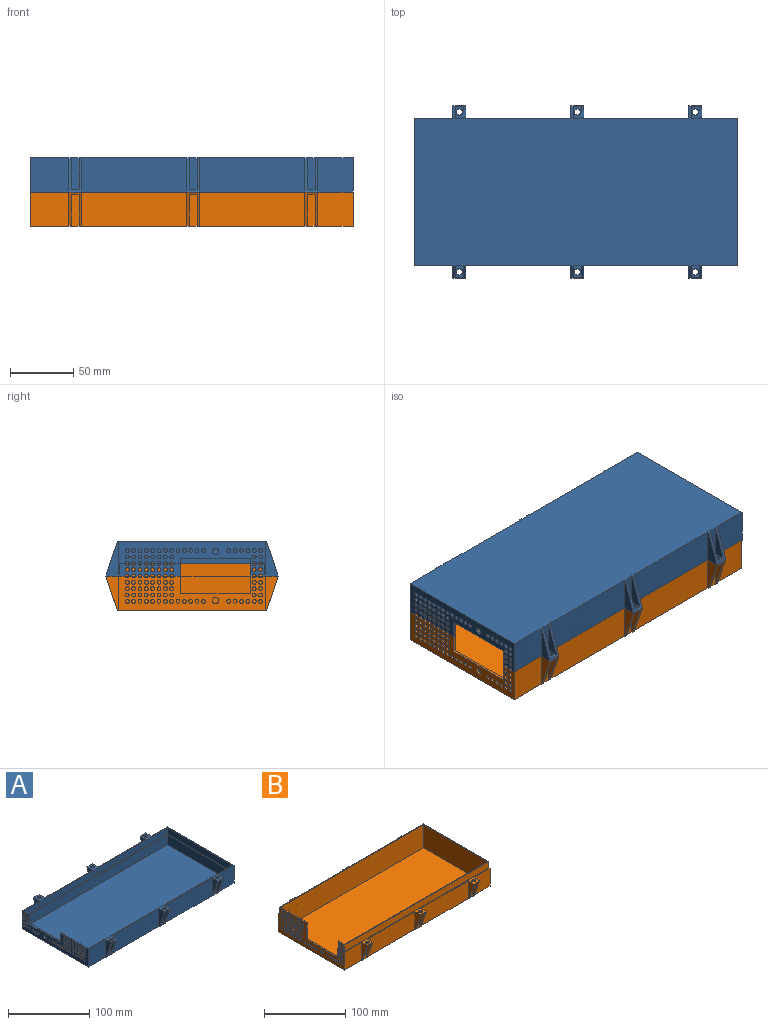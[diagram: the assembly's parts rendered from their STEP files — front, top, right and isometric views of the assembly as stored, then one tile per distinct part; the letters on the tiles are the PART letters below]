
ASSEMBLY  parts=2 mates=1
PART A: 154 faces, bbox 254x136x27 mm
  f0: plane 252.2x114.2mm, normal (0,0,1), area 671.6mm2, adj f20,f23,f41,f42,f43,f44,f45,f46
  f1: plane 2x1.2mm, normal (0,0,1), area 2.4mm2, adj f20,f23,f108,f109
  f2: plane 2x1.2mm, normal (0,0,1), area 2.4mm2, adj f20,f23,f107,f108
  f3: plane 2x1.2mm, normal (0,0,1), area 2.4mm2, adj f20,f23,f106,f107
  f4: plane 2x1.2mm, normal (0,0,1), area 2.4mm2, adj f20,f23,f105,f106
  f5: plane 2x1.2mm, normal (0,0,1), area 2.4mm2, adj f20,f23,f104,f105
  f6: plane 2x1.2mm, normal (0,0,1), area 2.4mm2, adj f20,f23,f103,f104
  f7: plane 2x1.2mm, normal (0,0,1), area 2.4mm2, adj f20,f23,f102,f103
  f8: plane 1.5x1.2mm, normal (0,0,1), area 1.8mm2, adj f20,f44,f93,f96
  f9: plane 2x1.2mm, normal (0,0,1), area 2.4mm2, adj f20,f44,f95,f96
  f10: plane 1.5x0.9mm, normal (0,0,1), area 1.3mm2, adj f37,f44,f93,f100
  f11: plane 2x0.9mm, normal (0,0,1), area 1.8mm2, adj f37,f44,f98,f100
  f12: plane 2x0.9mm, normal (0,0,1), area 1.8mm2, adj f23,f37,f134,f140
  f13: plane 2x0.9mm, normal (0,0,1), area 1.8mm2, adj f23,f37,f138,f140
  f14: plane 254x136mm, normal (0,0,1), area 1047.8mm2, adj f23,f25,f27,f29,f30,f32,f34,f36
  f15: plane 2x0.9mm, normal (0,0,1), area 1.8mm2, adj f23,f37,f134,f136
  f16: plane 2x0.9mm, normal (0,0,1), area 1.8mm2, adj f23,f37,f127,f132
  f17: plane 2x0.9mm, normal (0,0,1), area 1.8mm2, adj f23,f37,f130,f132
  f18: plane 2x0.9mm, normal (0,0,1), area 1.8mm2, adj f23,f37,f129,f138
  f19: plane 2x0.9mm, normal (0,0,1), area 1.8mm2, adj f23,f37,f127,f129
  f20: plane 112x15mm, normal (1,0,0), area 1200mm2, adj f0,f1,f2,f3,f4,f5,f6,f7
  f21: plane 5.5x1.2mm, normal (0,0,1), area 6.6mm2, adj f20,f23,f92,f102
  f22: plane 5.5x0.9mm, normal (0,0,1), area 4.9mm2, adj f23,f37,f92,f130
  f23: plane 48.1x10mm, normal (1,0,0), area 367.9mm2, adj f0,f1,f2,f3,f4,f5,f6,f7
  f24: plane 25x6mm, normal (0,1,0), area 150mm2, adj f40,f84,f88,f89
  f25: plane 28x27mm, normal (0,1,0), area 756mm2, adj f14,f39,f40,f87
  f26: plane 25x6mm, normal (0,1,0), area 150mm2, adj f40,f77,f81,f82
  f27: plane 83x27mm, normal (0,1,0), area 2241mm2, adj f14,f40,f80,f85
  f28: plane 25x6mm, normal (0,1,0), area 150mm2, adj f40,f70,f74,f75
  f29: plane 83x27mm, normal (0,1,0), area 2241mm2, adj f14,f40,f73,f78
  f30: plane 28x27mm, normal (0,-1,0), area 756mm2, adj f14,f39,f40,f66
  f31: plane 25x6mm, normal (0,-1,0), area 150mm2, adj f40,f63,f67,f68
  f32: plane 83x27mm, normal (0,-1,0), area 2241mm2, adj f14,f40,f59,f64
  f33: plane 25x6mm, normal (0,-1,0), area 150mm2, adj f40,f56,f60,f61
  f34: plane 83x27mm, normal (0,-1,0), area 2241mm2, adj f14,f40,f52,f57
  f35: plane 25x6mm, normal (0,-1,0), area 150mm2, adj f40,f49,f53,f54
  f36: plane 30x27mm, normal (0,1,0), area 810mm2, adj f14,f37,f40,f71
  f37: plane 116x27mm, normal (-1,0,0), area 1960.7mm2, adj f10,f11,f12,f13,f14,f15,f16,f17
  f38: plane 30x27mm, normal (0,-1,0), area 810mm2, adj f14,f37,f40,f50
  f39: plane 116x27mm, normal (1,0,0), area 3132mm2, adj f14,f25,f30,f40
  f40: plane 254x117.41mm, normal (0,0,-1), area 29480.9mm2, adj f24,f25,f26,f27,f28,f29,f30,f31
  f41: plane 252.2x10mm, normal (0,1,0), area 2522mm2, adj f0,f14,f23,f42
  f42: plane 114.2x10mm, normal (-1,0,0), area 1142mm2, adj f0,f14,f41,f43
  f43: plane 252.2x10mm, normal (0,-1,0), area 2522mm2, adj f0,f14,f42,f44
  f44: plane 11.1x10mm, normal (1,0,0), area 82.7mm2, adj f0,f8,f9,f10,f11,f14,f43,f93
  f45: plane 250x15mm, normal (0,1,0), area 3750mm2, adj f0,f20,f46,f48
  f46: plane 112x15mm, normal (-1,0,0), area 1680mm2, adj f0,f45,f47,f48
  f47: plane 250x15mm, normal (0,-1,0), area 3750mm2, adj f0,f20,f46,f48
  f48: plane 250x112mm, normal (0,0,1), area 28000mm2, adj f20,f45,f46,f47
  f49: plane 9.31x6mm, normal (0,0,-1), area 36.2mm2, adj f35,f51,f53,f54,f55
  f50: plane 27x10mm, normal (-1,0,0), area 144.5mm2, adj f14,f38,f40,f51
  f51: plane 27x10mm, normal (0,-0.95,-0.33), area 126.9mm2, adj f14,f40,f49,f50,f52,f53,f54
  f52: plane 27x10mm, normal (1,0,0), area 144.5mm2, adj f14,f34,f40,f51
  f53: plane 25x9.31mm, normal (1,0,0), area 125.2mm2, adj f35,f40,f49,f51
  f54: plane 25x9.31mm, normal (-1,0,0), area 125.2mm2, adj f35,f40,f49,f51
  f55: cylinder r=2.5mm len=5mm, axis (0,0,1), area 31.4mm2, adj f14,f49
  f56: plane 9.31x6mm, normal (0,0,-1), area 36.2mm2, adj f33,f58,f60,f61,f62
  f57: plane 27x10mm, normal (-1,0,0), area 144.5mm2, adj f14,f34,f40,f58
  f58: plane 27x10mm, normal (0,-0.95,-0.33), area 126.9mm2, adj f14,f40,f56,f57,f59,f60,f61
  f59: plane 27x10mm, normal (1,0,0), area 144.5mm2, adj f14,f32,f40,f58
  f60: plane 25x9.31mm, normal (1,0,0), area 125.2mm2, adj f33,f40,f56,f58
  f61: plane 25x9.31mm, normal (-1,0,0), area 125.2mm2, adj f33,f40,f56,f58
  f62: cylinder r=2.5mm len=5mm, axis (0,0,1), area 31.4mm2, adj f14,f56
  f63: plane 9.31x6mm, normal (0,0,-1), area 36.2mm2, adj f31,f65,f67,f68,f69
  f64: plane 27x10mm, normal (-1,0,0), area 144.5mm2, adj f14,f32,f40,f65
  f65: plane 27x10mm, normal (0,-0.95,-0.33), area 126.9mm2, adj f14,f40,f63,f64,f66,f67,f68
  f66: plane 27x10mm, normal (1,0,0), area 144.5mm2, adj f14,f30,f40,f65
  f67: plane 25x9.31mm, normal (1,0,0), area 125.2mm2, adj f31,f40,f63,f65
  f68: plane 25x9.31mm, normal (-1,0,0), area 125.2mm2, adj f31,f40,f63,f65
  f69: cylinder r=2.5mm len=5mm, axis (0,0,1), area 31.4mm2, adj f14,f63
  f70: plane 9.31x6mm, normal (0,0,-1), area 36.2mm2, adj f28,f72,f74,f75,f76
  f71: plane 27x10mm, normal (-1,0,0), area 144.5mm2, adj f14,f36,f40,f72
  f72: plane 27x10mm, normal (0,0.95,-0.33), area 126.9mm2, adj f14,f40,f70,f71,f73,f74,f75
  f73: plane 27x10mm, normal (1,0,0), area 144.5mm2, adj f14,f29,f40,f72
  f74: plane 25x9.31mm, normal (1,0,0), area 125.2mm2, adj f28,f40,f70,f72
  f75: plane 25x9.31mm, normal (-1,0,0), area 125.2mm2, adj f28,f40,f70,f72
  f76: cylinder r=2.5mm len=5mm, axis (0,0,1), area 31.4mm2, adj f14,f70
  f77: plane 9.31x6mm, normal (0,0,-1), area 36.2mm2, adj f26,f79,f81,f82,f83
  f78: plane 27x10mm, normal (-1,0,0), area 144.5mm2, adj f14,f29,f40,f79
  f79: plane 27x10mm, normal (0,0.95,-0.33), area 126.9mm2, adj f14,f40,f77,f78,f80,f81,f82
  f80: plane 27x10mm, normal (1,0,0), area 144.5mm2, adj f14,f27,f40,f79
  f81: plane 25x9.31mm, normal (1,0,0), area 125.2mm2, adj f26,f40,f77,f79
  f82: plane 25x9.31mm, normal (-1,0,0), area 125.2mm2, adj f26,f40,f77,f79
  f83: cylinder r=2.5mm len=5mm, axis (0,0,1), area 31.4mm2, adj f14,f77
  f84: plane 9.31x6mm, normal (0,0,-1), area 36.2mm2, adj f24,f86,f88,f89,f90
  f85: plane 27x10mm, normal (-1,0,0), area 144.5mm2, adj f14,f27,f40,f86
  f86: plane 27x10mm, normal (0,0.95,-0.33), area 126.9mm2, adj f14,f40,f84,f85,f87,f88,f89
  f87: plane 27x10mm, normal (1,0,0), area 144.5mm2, adj f14,f25,f40,f86
  f88: plane 25x9.31mm, normal (1,0,0), area 125.2mm2, adj f24,f40,f84,f86
  f89: plane 25x9.31mm, normal (-1,0,0), area 125.2mm2, adj f24,f40,f84,f86
  f90: cylinder r=2.5mm len=5mm, axis (0,0,1), area 31.4mm2, adj f14,f84
  f91: plane 55x2.1mm, normal (0,0,1), area 115.5mm2, adj f20,f37,f92,f93
  f92: plane 14x2.1mm, normal (0,1,0), area 17.4mm2, adj f20,f21,f22,f23,f37,f91
  f93: plane 14x2.1mm, normal (0,-1,0), area 17.4mm2, adj f8,f10,f20,f37,f44,f91
  f94: cylinder r=2.5mm len=5mm, axis (-1,0,0), area 33mm2, adj f20,f37
  f95: cylinder r=1.5mm len=3mm, axis (1,0,0), area 14.1mm2, adj f0,f9,f20,f37,f44
  f96: cylinder r=1.5mm len=3mm, axis (1,0,0), area 14.1mm2, adj f8,f9,f20,f37,f44
  f97: cylinder r=1.5mm len=3mm, axis (1,0,0), area 8.5mm2, adj f37,f44
  f98: cylinder r=1.5mm len=3mm, axis (1,0,0), area 4.2mm2, adj f11,f14,f37,f44
  f99: cylinder r=1.5mm len=3mm, axis (1,0,0), area 8.5mm2, adj f37,f44
  f100: cylinder r=1.5mm len=3mm, axis (1,0,0), area 4.2mm2, adj f10,f11,f37,f44
  f101: cylinder r=1.5mm len=3mm, axis (1,0,0), area 8.5mm2, adj f23,f37
  f102: cylinder r=1.5mm len=3mm, axis (1,0,0), area 14.1mm2, adj f7,f20,f21,f23,f37
  f103: cylinder r=1.5mm len=3mm, axis (1,0,0), area 14.1mm2, adj f6,f7,f20,f23,f37
  f104: cylinder r=1.5mm len=3mm, axis (1,0,0), area 14.1mm2, adj f5,f6,f20,f23,f37
  f105: cylinder r=1.5mm len=3mm, axis (1,0,0), area 14.1mm2, adj f4,f5,f20,f23,f37
  f106: cylinder r=1.5mm len=3mm, axis (1,0,0), area 14.1mm2, adj f3,f4,f20,f23,f37
  f107: cylinder r=1.5mm len=3mm, axis (1,0,0), area 14.1mm2, adj f2,f3,f20,f23,f37
  f108: cylinder r=1.5mm len=3mm, axis (1,0,0), area 14.1mm2, adj f1,f2,f20,f23,f37
  f109: cylinder r=1.5mm len=3mm, axis (1,0,0), area 14.1mm2, adj f0,f1,f20,f23,f37
  f110: cylinder r=1.5mm len=3mm, axis (1,0,0), area 19.8mm2, adj f20,f37
  f111: cylinder r=1.5mm len=3mm, axis (1,0,0), area 19.8mm2, adj f20,f37
  f112: cylinder r=1.5mm len=3mm, axis (1,0,0), area 19.8mm2, adj f20,f37
  f113: cylinder r=1.5mm len=3mm, axis (1,0,0), area 19.8mm2, adj f20,f37
  f114: cylinder r=1.5mm len=3mm, axis (1,0,0), area 19.8mm2, adj f20,f37
  f115: cylinder r=1.5mm len=3mm, axis (1,0,0), area 19.8mm2, adj f20,f37
  f116: cylinder r=1.5mm len=3mm, axis (1,0,0), area 19.8mm2, adj f20,f37
  f117: cylinder r=1.5mm len=3mm, axis (1,0,0), area 19.8mm2, adj f20,f37
  f118: cylinder r=1.5mm len=3mm, axis (1,0,0), area 19.8mm2, adj f20,f37
  f119: cylinder r=1.5mm len=3mm, axis (1,0,0), area 19.8mm2, adj f20,f37
  f120: cylinder r=1.5mm len=3mm, axis (1,0,0), area 19.8mm2, adj f20,f37
  f121: cylinder r=1.5mm len=3mm, axis (1,0,0), area 19.8mm2, adj f20,f37
  f122: cylinder r=1.5mm len=3mm, axis (1,0,0), area 19.8mm2, adj f20,f37
  f123: cylinder r=1.5mm len=3mm, axis (1,0,0), area 19.8mm2, adj f20,f37
  f124: cylinder r=1.5mm len=3mm, axis (1,0,0), area 19.8mm2, adj f20,f37
  f125: cylinder r=1.5mm len=3mm, axis (1,0,0), area 19.8mm2, adj f20,f37
  f126: cylinder r=1.5mm len=3mm, axis (1,0,0), area 8.5mm2, adj f23,f37
  f127: cylinder r=1.5mm len=3mm, axis (1,0,0), area 4.2mm2, adj f16,f19,f23,f37
  f128: cylinder r=1.5mm len=3mm, axis (1,0,0), area 8.5mm2, adj f23,f37
  f129: cylinder r=1.5mm len=3mm, axis (1,0,0), area 4.2mm2, adj f18,f19,f23,f37
  f130: cylinder r=1.5mm len=3mm, axis (1,0,0), area 4.2mm2, adj f17,f22,f23,f37
  f131: cylinder r=1.5mm len=3mm, axis (1,0,0), area 8.5mm2, adj f23,f37
  f132: cylinder r=1.5mm len=3mm, axis (1,0,0), area 4.2mm2, adj f16,f17,f23,f37
  f133: cylinder r=1.5mm len=3mm, axis (1,0,0), area 8.5mm2, adj f23,f37
  f134: cylinder r=1.5mm len=3mm, axis (1,0,0), area 4.2mm2, adj f12,f15,f23,f37
  f135: cylinder r=1.5mm len=3mm, axis (1,0,0), area 8.5mm2, adj f23,f37
  f136: cylinder r=1.5mm len=3mm, axis (1,0,0), area 4.2mm2, adj f14,f15,f23,f37
  f137: cylinder r=1.5mm len=3mm, axis (1,0,0), area 8.5mm2, adj f23,f37
  f138: cylinder r=1.5mm len=3mm, axis (1,0,0), area 4.2mm2, adj f13,f18,f23,f37
  f139: cylinder r=1.5mm len=3mm, axis (1,0,0), area 8.5mm2, adj f23,f37
  f140: cylinder r=1.5mm len=3mm, axis (1,0,0), area 4.2mm2, adj f12,f13,f23,f37
  f141: cylinder r=1.5mm len=3mm, axis (1,0,0), area 19.8mm2, adj f20,f37
  f142: cylinder r=1.5mm len=3mm, axis (1,0,0), area 19.8mm2, adj f20,f37
  f143: cylinder r=1.5mm len=3mm, axis (1,0,0), area 19.8mm2, adj f20,f37
  f144: cylinder r=1.5mm len=3mm, axis (1,0,0), area 19.8mm2, adj f20,f37
  f145: cylinder r=1.5mm len=3mm, axis (1,0,0), area 19.8mm2, adj f20,f37
  f146: cylinder r=1.5mm len=3mm, axis (1,0,0), area 19.8mm2, adj f20,f37
  f147: cylinder r=1.5mm len=3mm, axis (1,0,0), area 19.8mm2, adj f20,f37
  f148: cylinder r=1.5mm len=3mm, axis (1,0,0), area 19.8mm2, adj f20,f37
  f149: cylinder r=1.5mm len=3mm, axis (1,0,0), area 19.8mm2, adj f20,f37
  f150: cylinder r=1.5mm len=3mm, axis (1,0,0), area 19.8mm2, adj f20,f37
  f151: cylinder r=1.5mm len=3mm, axis (1,0,0), area 19.8mm2, adj f20,f37
  f152: cylinder r=1.5mm len=3mm, axis (1,0,0), area 19.8mm2, adj f20,f37
  f153: cylinder r=1.5mm len=3mm, axis (1,0,0), area 19.8mm2, adj f20,f37
PART B: 175 faces, bbox 254x136x37 mm
  f0: plane 2x1mm, normal (0,0,1), area 2mm2, adj f24,f43,f115,f117
  f1: plane 2x1mm, normal (0,0,1), area 2mm2, adj f24,f43,f106,f115
  f2: plane 2x1mm, normal (0,0,1), area 2mm2, adj f24,f43,f112,f114
  f3: plane 2x1mm, normal (0,0,1), area 2mm2, adj f24,f43,f112,f117
  f4: plane 2x1mm, normal (0,0,1), area 2mm2, adj f24,f43,f108,f110
  f5: plane 252x114mm, normal (0,0,1), area 620mm2, adj f22,f24,f41,f42,f43,f44,f45,f46
  f6: plane 2x1mm, normal (0,0,1), area 2mm2, adj f24,f43,f104,f106
  f7: plane 2x1mm, normal (0,0,1), area 2mm2, adj f24,f43,f104,f110
  f8: plane 2x1mm, normal (0,0,1), area 2mm2, adj f22,f24,f170,f172
  f9: plane 1.5x1mm, normal (0,0,1), area 1.5mm2, adj f22,f24,f92,f170
  f10: plane 2x1mm, normal (0,0,1), area 2mm2, adj f20,f22,f168,f169
  f11: plane 1.5x1mm, normal (0,0,1), area 1.5mm2, adj f20,f22,f92,f168
  f12: plane 2x1mm, normal (0,0,1), area 2mm2, adj f20,f43,f102,f103
  f13: plane 2x1mm, normal (0,0,1), area 2mm2, adj f20,f43,f101,f102
  f14: plane 2x1mm, normal (0,0,1), area 2mm2, adj f20,f43,f100,f101
  f15: plane 2x1mm, normal (0,0,1), area 2mm2, adj f20,f43,f99,f100
  f16: plane 2x1mm, normal (0,0,1), area 2mm2, adj f20,f43,f98,f99
  f17: plane 2x1mm, normal (0,0,1), area 2mm2, adj f20,f43,f97,f98
  f18: plane 2x1mm, normal (0,0,1), area 2mm2, adj f20,f43,f96,f97
  f19: plane 254x136mm, normal (0,0,1), area 1110.2mm2, adj f20,f22,f26,f28,f30,f31,f33,f35
  f20: plane 116x27mm, normal (-1,0,0), area 1960.7mm2, adj f10,f11,f12,f13,f14,f15,f16,f17
  f21: plane 5.5x1mm, normal (0,0,1), area 5.5mm2, adj f24,f43,f93,f114
  f22: plane 11x10mm, normal (-1,0,0), area 81.7mm2, adj f5,f8,f9,f10,f11,f19,f42,f92
  f23: plane 5.5x1mm, normal (0,0,1), area 5.5mm2, adj f20,f43,f93,f103
  f24: plane 112x35mm, normal (1,0,0), area 2057.3mm2, adj f0,f1,f2,f3,f4,f5,f6,f7
  f25: plane 25x6mm, normal (0,1,0), area 150mm2, adj f40,f84,f88,f89
  f26: plane 28x27mm, normal (0,1,0), area 756mm2, adj f19,f39,f40,f87
  f27: plane 25x6mm, normal (0,1,0), area 150mm2, adj f40,f77,f81,f82
  f28: plane 83x27mm, normal (0,1,0), area 2241mm2, adj f19,f40,f80,f85
  f29: plane 25x6mm, normal (0,1,0), area 150mm2, adj f40,f70,f74,f75
  f30: plane 83x27mm, normal (0,1,0), area 2241mm2, adj f19,f40,f73,f78
  f31: plane 28x27mm, normal (0,-1,0), area 756mm2, adj f19,f39,f40,f66
  f32: plane 25x6mm, normal (0,-1,0), area 150mm2, adj f40,f63,f67,f68
  f33: plane 83x27mm, normal (0,-1,0), area 2241mm2, adj f19,f40,f59,f64
  f34: plane 25x6mm, normal (0,-1,0), area 150mm2, adj f40,f56,f60,f61
  f35: plane 83x27mm, normal (0,-1,0), area 2241mm2, adj f19,f40,f52,f57
  f36: plane 25x6mm, normal (0,-1,0), area 150mm2, adj f40,f49,f53,f54
  f37: plane 30x27mm, normal (0,1,0), area 731.5mm2, adj f19,f20,f40,f71,f174
  f38: plane 30x27mm, normal (0,-1,0), area 810mm2, adj f19,f20,f40,f50
  f39: plane 116x27mm, normal (1,0,0), area 3132mm2, adj f19,f26,f31,f40
  f40: plane 254x117.41mm, normal (0,0,-1), area 29480.9mm2, adj f20,f25,f26,f27,f28,f29,f30,f31
  f41: plane 114x10mm, normal (1,0,0), area 1140mm2, adj f5,f19,f42,f44
  f42: plane 252x10mm, normal (0,-1,0), area 2520mm2, adj f5,f19,f22,f41
  f43: plane 48x10mm, normal (-1,0,0), area 366.9mm2, adj f0,f1,f2,f3,f4,f5,f6,f7
  f44: plane 252x10mm, normal (0,1,0), area 2520mm2, adj f5,f19,f41,f43
  f45: plane 250x35mm, normal (0,1,0), area 8750mm2, adj f5,f24,f46,f48
  f46: plane 112x35mm, normal (-1,0,0), area 3920mm2, adj f5,f45,f47,f48
  f47: plane 250x35mm, normal (0,-1,0), area 8671.5mm2, adj f5,f24,f46,f48,f174
  f48: plane 250x112mm, normal (0,0,1), area 28000mm2, adj f24,f45,f46,f47
  f49: plane 9.31x6mm, normal (0,0,-1), area 36.2mm2, adj f36,f51,f53,f54,f55
  f50: plane 27x10mm, normal (-1,0,0), area 144.5mm2, adj f19,f38,f40,f51
  f51: plane 27x10mm, normal (0,-0.95,-0.33), area 126.9mm2, adj f19,f40,f49,f50,f52,f53,f54
  f52: plane 27x10mm, normal (1,0,0), area 144.5mm2, adj f19,f35,f40,f51
  f53: plane 25x9.31mm, normal (1,0,0), area 125.2mm2, adj f36,f40,f49,f51
  f54: plane 25x9.31mm, normal (-1,0,0), area 125.2mm2, adj f36,f40,f49,f51
  f55: cylinder r=2.5mm len=5mm, axis (0,0,1), area 31.4mm2, adj f19,f49
  f56: plane 9.31x6mm, normal (0,0,-1), area 36.2mm2, adj f34,f58,f60,f61,f62
  f57: plane 27x10mm, normal (-1,0,0), area 144.5mm2, adj f19,f35,f40,f58
  f58: plane 27x10mm, normal (0,-0.95,-0.33), area 126.9mm2, adj f19,f40,f56,f57,f59,f60,f61
  f59: plane 27x10mm, normal (1,0,0), area 144.5mm2, adj f19,f33,f40,f58
  f60: plane 25x9.31mm, normal (1,0,0), area 125.2mm2, adj f34,f40,f56,f58
  f61: plane 25x9.31mm, normal (-1,0,0), area 125.2mm2, adj f34,f40,f56,f58
  f62: cylinder r=2.5mm len=5mm, axis (0,0,1), area 31.4mm2, adj f19,f56
  f63: plane 9.31x6mm, normal (0,0,-1), area 36.2mm2, adj f32,f65,f67,f68,f69
  f64: plane 27x10mm, normal (-1,0,0), area 144.5mm2, adj f19,f33,f40,f65
  f65: plane 27x10mm, normal (0,-0.95,-0.33), area 126.9mm2, adj f19,f40,f63,f64,f66,f67,f68
  f66: plane 27x10mm, normal (1,0,0), area 144.5mm2, adj f19,f31,f40,f65
  f67: plane 25x9.31mm, normal (1,0,0), area 125.2mm2, adj f32,f40,f63,f65
  f68: plane 25x9.31mm, normal (-1,0,0), area 125.2mm2, adj f32,f40,f63,f65
  f69: cylinder r=2.5mm len=5mm, axis (0,0,1), area 31.4mm2, adj f19,f63
  f70: plane 9.31x6mm, normal (0,0,-1), area 36.2mm2, adj f29,f72,f74,f75,f76
  f71: plane 27x10mm, normal (-1,0,0), area 144.5mm2, adj f19,f37,f40,f72
  f72: plane 27x10mm, normal (0,0.95,-0.33), area 126.9mm2, adj f19,f40,f70,f71,f73,f74,f75
  f73: plane 27x10mm, normal (1,0,0), area 144.5mm2, adj f19,f30,f40,f72
  f74: plane 25x9.31mm, normal (1,0,0), area 125.2mm2, adj f29,f40,f70,f72
  f75: plane 25x9.31mm, normal (-1,0,0), area 125.2mm2, adj f29,f40,f70,f72
  f76: cylinder r=2.5mm len=5mm, axis (0,0,1), area 31.4mm2, adj f19,f70
  f77: plane 9.31x6mm, normal (0,0,-1), area 36.2mm2, adj f27,f79,f81,f82,f83
  f78: plane 27x10mm, normal (-1,0,0), area 144.5mm2, adj f19,f30,f40,f79
  f79: plane 27x10mm, normal (0,0.95,-0.33), area 126.9mm2, adj f19,f40,f77,f78,f80,f81,f82
  f80: plane 27x10mm, normal (1,0,0), area 144.5mm2, adj f19,f28,f40,f79
  f81: plane 25x9.31mm, normal (1,0,0), area 125.2mm2, adj f27,f40,f77,f79
  f82: plane 25x9.31mm, normal (-1,0,0), area 125.2mm2, adj f27,f40,f77,f79
  f83: cylinder r=2.5mm len=5mm, axis (0,0,1), area 31.4mm2, adj f19,f77
  f84: plane 9.31x6mm, normal (0,0,-1), area 36.2mm2, adj f25,f86,f88,f89,f90
  f85: plane 27x10mm, normal (-1,0,0), area 144.5mm2, adj f19,f28,f40,f86
  f86: plane 27x10mm, normal (0,0.95,-0.33), area 126.9mm2, adj f19,f40,f84,f85,f87,f88,f89
  f87: plane 27x10mm, normal (1,0,0), area 144.5mm2, adj f19,f26,f40,f86
  f88: plane 25x9.31mm, normal (1,0,0), area 125.2mm2, adj f25,f40,f84,f86
  f89: plane 25x9.31mm, normal (-1,0,0), area 125.2mm2, adj f25,f40,f84,f86
  f90: cylinder r=2.5mm len=5mm, axis (0,0,1), area 31.4mm2, adj f19,f84
  f91: plane 55x2mm, normal (0,0,1), area 110mm2, adj f20,f24,f92,f93
  f92: plane 24x2mm, normal (0,1,0), area 38mm2, adj f9,f11,f20,f22,f24,f91
  f93: plane 24x2mm, normal (0,-1,0), area 38mm2, adj f20,f21,f23,f24,f43,f91
  f94: cylinder r=2.5mm len=5mm, axis (-1,0,0), area 31.4mm2, adj f20,f24
  f95: cylinder r=1.5mm len=3mm, axis (-1,0,0), area 9.4mm2, adj f24,f43
  f96: cylinder r=1.5mm len=3mm, axis (-1,0,0), area 14.1mm2, adj f18,f19,f20,f24,f43
  f97: cylinder r=1.5mm len=3mm, axis (-1,0,0), area 14.1mm2, adj f17,f18,f20,f24,f43
  f98: cylinder r=1.5mm len=3mm, axis (-1,0,0), area 14.1mm2, adj f16,f17,f20,f24,f43
  f99: cylinder r=1.5mm len=3mm, axis (-1,0,0), area 14.1mm2, adj f15,f16,f20,f24,f43
  f100: cylinder r=1.5mm len=3mm, axis (-1,0,0), area 14.1mm2, adj f14,f15,f20,f24,f43
  f101: cylinder r=1.5mm len=3mm, axis (-1,0,0), area 14.1mm2, adj f13,f14,f20,f24,f43
  f102: cylinder r=1.5mm len=3mm, axis (-1,0,0), area 14.1mm2, adj f12,f13,f20,f24,f43
  f103: cylinder r=1.5mm len=3mm, axis (-1,0,0), area 14.1mm2, adj f12,f20,f23,f24,f43
  f104: cylinder r=1.5mm len=3mm, axis (-1,0,0), area 4.7mm2, adj f6,f7,f24,f43
  f105: cylinder r=1.5mm len=3mm, axis (-1,0,0), area 9.4mm2, adj f24,f43
  f106: cylinder r=1.5mm len=3mm, axis (-1,0,0), area 4.7mm2, adj f1,f6,f24,f43
  f107: cylinder r=1.5mm len=3mm, axis (-1,0,0), area 9.4mm2, adj f24,f43
  f108: cylinder r=1.5mm len=3mm, axis (-1,0,0), area 4.7mm2, adj f4,f5,f24,f43
  f109: cylinder r=1.5mm len=3mm, axis (-1,0,0), area 9.4mm2, adj f24,f43
  f110: cylinder r=1.5mm len=3mm, axis (-1,0,0), area 4.7mm2, adj f4,f7,f24,f43
  f111: cylinder r=1.5mm len=3mm, axis (-1,0,0), area 9.4mm2, adj f24,f43
  f112: cylinder r=1.5mm len=3mm, axis (-1,0,0), area 4.7mm2, adj f2,f3,f24,f43
  f113: cylinder r=1.5mm len=3mm, axis (-1,0,0), area 9.4mm2, adj f24,f43
  f114: cylinder r=1.5mm len=3mm, axis (-1,0,0), area 4.7mm2, adj f2,f21,f24,f43
  f115: cylinder r=1.5mm len=3mm, axis (-1,0,0), area 4.7mm2, adj f0,f1,f24,f43
  f116: cylinder r=1.5mm len=3mm, axis (-1,0,0), area 9.4mm2, adj f24,f43
  f117: cylinder r=1.5mm len=3mm, axis (-1,0,0), area 4.7mm2, adj f0,f3,f24,f43
  f118: cylinder r=1.5mm len=3mm, axis (-1,0,0), area 9.4mm2, adj f24,f43
  f119: cylinder r=1.5mm len=3mm, axis (-1,0,0), area 18.8mm2, adj f20,f24
  f120: cylinder r=1.5mm len=3mm, axis (-1,0,0), area 18.8mm2, adj f20,f24
  f121: cylinder r=1.5mm len=3mm, axis (-1,0,0), area 18.8mm2, adj f20,f24
  f122: cylinder r=1.5mm len=3mm, axis (-1,0,0), area 18.8mm2, adj f20,f24
  f123: cylinder r=1.5mm len=3mm, axis (-1,0,0), area 18.8mm2, adj f20,f24
  f124: cylinder r=1.5mm len=3mm, axis (-1,0,0), area 18.8mm2, adj f20,f24
  f125: cylinder r=1.5mm len=3mm, axis (-1,0,0), area 18.8mm2, adj f20,f24
  f126: cylinder r=1.5mm len=3mm, axis (-1,0,0), area 18.8mm2, adj f20,f24
  f127: cylinder r=1.5mm len=3mm, axis (-1,0,0), area 18.8mm2, adj f20,f24
  f128: cylinder r=1.5mm len=3mm, axis (-1,0,0), area 18.8mm2, adj f20,f24
  f129: cylinder r=1.5mm len=3mm, axis (-1,0,0), area 18.8mm2, adj f20,f24
  f130: cylinder r=1.5mm len=3mm, axis (-1,0,0), area 18.8mm2, adj f20,f24
  f131: cylinder r=1.5mm len=3mm, axis (-1,0,0), area 18.8mm2, adj f20,f24
  f132: cylinder r=1.5mm len=3mm, axis (-1,0,0), area 18.8mm2, adj f20,f24
  f133: cylinder r=1.5mm len=3mm, axis (-1,0,0), area 18.8mm2, adj f20,f24
  f134: cylinder r=1.5mm len=3mm, axis (-1,0,0), area 18.8mm2, adj f20,f24
  f135: cylinder r=1.5mm len=3mm, axis (-1,0,0), area 18.8mm2, adj f20,f24
  f136: cylinder r=1.5mm len=3mm, axis (-1,0,0), area 18.8mm2, adj f20,f24
  f137: cylinder r=1.5mm len=3mm, axis (-1,0,0), area 18.8mm2, adj f20,f24
  f138: cylinder r=1.5mm len=3mm, axis (-1,0,0), area 18.8mm2, adj f20,f24
  f139: cylinder r=1.5mm len=3mm, axis (-1,0,0), area 18.8mm2, adj f20,f24
  f140: cylinder r=1.5mm len=3mm, axis (-1,0,0), area 18.8mm2, adj f20,f24
  f141: cylinder r=1.5mm len=3mm, axis (-1,0,0), area 18.8mm2, adj f20,f24
  f142: cylinder r=1.5mm len=3mm, axis (-1,0,0), area 18.8mm2, adj f20,f24
  f143: cylinder r=1.5mm len=3mm, axis (-1,0,0), area 18.8mm2, adj f20,f24
  f144: cylinder r=1.5mm len=3mm, axis (-1,0,0), area 18.8mm2, adj f20,f24
  f145: cylinder r=1.5mm len=3mm, axis (-1,0,0), area 18.8mm2, adj f20,f24
  f146: cylinder r=1.5mm len=3mm, axis (-1,0,0), area 18.8mm2, adj f20,f24
  f147: cylinder r=1.5mm len=3mm, axis (-1,0,0), area 18.8mm2, adj f20,f24
  f148: cylinder r=1.5mm len=3mm, axis (-1,0,0), area 18.8mm2, adj f20,f24
  f149: cylinder r=1.5mm len=3mm, axis (-1,0,0), area 18.8mm2, adj f20,f24
  f150: cylinder r=1.5mm len=3mm, axis (-1,0,0), area 18.8mm2, adj f20,f24
  f151: cylinder r=1.5mm len=3mm, axis (-1,0,0), area 18.8mm2, adj f20,f24
  f152: cylinder r=1.5mm len=3mm, axis (-1,0,0), area 18.8mm2, adj f20,f24
  f153: cylinder r=1.5mm len=3mm, axis (-1,0,0), area 18.8mm2, adj f20,f24
  f154: cylinder r=1.5mm len=3mm, axis (-1,0,0), area 18.8mm2, adj f20,f24
  f155: cylinder r=1.5mm len=3mm, axis (-1,0,0), area 18.8mm2, adj f20,f24
  f156: cylinder r=1.5mm len=3mm, axis (-1,0,0), area 18.8mm2, adj f20,f24
  f157: cylinder r=1.5mm len=3mm, axis (-1,0,0), area 18.8mm2, adj f20,f24
  f158: cylinder r=1.5mm len=3mm, axis (-1,0,0), area 18.8mm2, adj f20,f24
  f159: cylinder r=1.5mm len=3mm, axis (-1,0,0), area 18.8mm2, adj f20,f24
  f160: cylinder r=1.5mm len=3mm, axis (-1,0,0), area 18.8mm2, adj f20,f24
  f161: cylinder r=1.5mm len=3mm, axis (-1,0,0), area 18.8mm2, adj f20,f24
  f162: cylinder r=1.5mm len=3mm, axis (-1,0,0), area 18.8mm2, adj f20,f24
  f163: cylinder r=1.5mm len=3mm, axis (-1,0,0), area 18.8mm2, adj f20,f24
  f164: cylinder r=1.5mm len=3mm, axis (-1,0,0), area 18.8mm2, adj f20,f24
  f165: cylinder r=1.5mm len=3mm, axis (-1,0,0), area 18.8mm2, adj f20,f24
  f166: cylinder r=1.5mm len=3mm, axis (-1,0,0), area 18.8mm2, adj f20,f24
  f167: cylinder r=1.5mm len=3mm, axis (-1,0,0), area 18.8mm2, adj f20,f24
  f168: cylinder r=1.5mm len=3mm, axis (-1,0,0), area 14.1mm2, adj f10,f11,f20,f22,f24
  f169: cylinder r=1.5mm len=3mm, axis (-1,0,0), area 14.1mm2, adj f10,f19,f20,f22,f24
  f170: cylinder r=1.5mm len=3mm, axis (-1,0,0), area 4.7mm2, adj f8,f9,f22,f24
  f171: cylinder r=1.5mm len=3mm, axis (-1,0,0), area 9.4mm2, adj f22,f24
  f172: cylinder r=1.5mm len=3mm, axis (-1,0,0), area 4.7mm2, adj f5,f8,f22,f24
  f173: cylinder r=1.5mm len=3mm, axis (-1,0,0), area 9.4mm2, adj f22,f24
  f174: cylinder r=5mm len=10mm, axis (0,1,0), area 62.8mm2, adj f37,f47
PLACE A rot(axis=(1,0,0),180deg) t=(-29.58,-62.09,42.56)mm
PLACE B t=(-29.58,46.13,-11.44)mm
MATE fastened A.f83 <-> B.f62  axis (0,0,-1) through (-20.97,-70.98,15.56)mm
